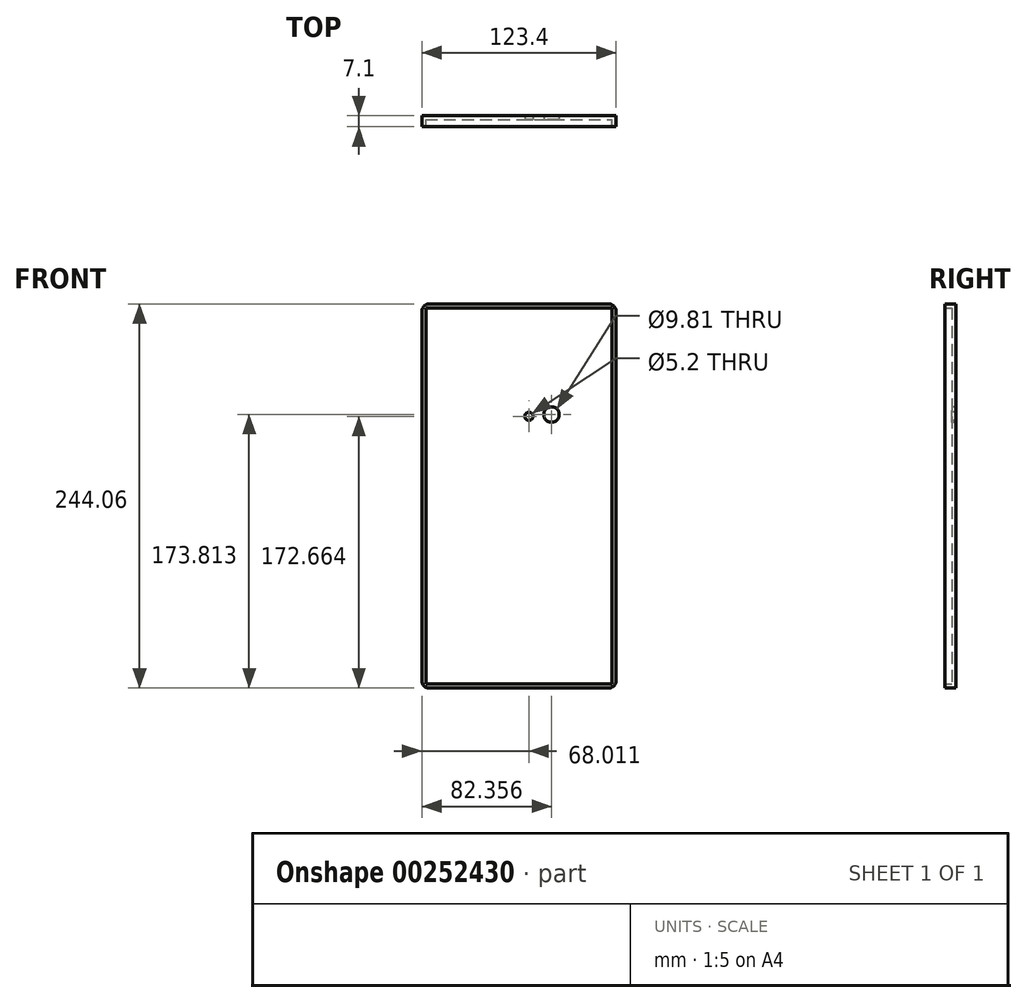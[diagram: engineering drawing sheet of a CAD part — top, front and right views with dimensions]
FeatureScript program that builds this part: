
annotation { "Feature Type Name" : "Feature", "Feature Type Description" : "" }
export const myFeature = defineFeature(function(context is Context, id is Id, definition is map)
    precondition{}
    {
        {
            var Q0;
            Q0=qCreatedBy(makeId("Front.planeOp"),FACE);
            var sketch = newSketch(context, id + "F0", { "sketchPlane" : qUnion([Q0])});
            skLineSegment(sketch, "E0.bottom", {"start": v(-61.7, 122.03) * mm, "end": v(61.7, 122.03) * mm});
            skLineSegment(sketch, "E0.top", {"start": v(-61.7, -122.03) * mm, "end": v(61.7, -122.03) * mm});
            skLineSegment(sketch, "E0.left", {"start": v(-61.7, 122.03) * mm, "end": v(-61.7, -122.03) * mm});
            skLineSegment(sketch, "E0.right", {"start": v(61.7, 122.03) * mm, "end": v(61.7, -122.03) * mm});
            skPoint(sketch, "E0.middle", {"position": v(0, 0) * mm});
            skSolve(sketch);
        }
        {
            var Q0;
            Q0=makeQuery(id+"F0.imprint","IMPRINT",FACE,{"disambiguationData":[TD([[makeQuery(id+"F0.imprint","IMPRINT",EDGE,{"derivedFrom":sQuery(id+"F0.wireOp",EDGE,"E0.bottom")}),-1.0]])]});
            extrude(context, id + "F1", {"entities" : qUnion([Q0]), "endBound" : BoundingType.SYMMETRIC, "depth" : 7.1 * mm});
        }
        {
            var Q0;
            Q0=makeQuery(id+"F1.opExtrude","CAP_FACE",FACE,{"disambiguationData":[OSD([sQuery(id+"F0.wireOp",EDGE,"E0.bottom"),sQuery(id+"F0.wireOp",EDGE,"E0.top"),sQuery(id+"F0.wireOp",EDGE,"E0.left"),sQuery(id+"F0.wireOp",EDGE,"E0.right")])],"isStart":false});
            shell(context, id + "F2", {"entities" : qUnion([Q0]), "thickness" : 2.54 * mm});
        }
        {
            var Q0;
            Q0=qCreatedBy(makeId("Front.planeOp"),FACE);
            var sketch = newSketch(context, id + "F3", { "sketchPlane" : qUnion([Q0])});
            skLineSegment(sketch, "E1.bottom", {"start": v(6.69, 50.63) * mm, "end": v(20.66, 50.63) * mm});
            skLineSegment(sketch, "E1.top", {"start": v(6.69, 50.63) * mm, "end": v(20.66, 50.63) * mm});
            skLineSegment(sketch, "E1.left", {"start": v(20.66, 50.63) * mm, "end": v(20.66, 50.63) * mm});
            skLineSegment(sketch, "E1.right", {"start": v(6.69, 50.63) * mm, "end": v(6.69, 50.63) * mm});
            skCircle(sketch, "E2", {"center": v(6.31, 50.63) * mm, "radius": 2.6 * mm});
            skPoint(sketch, "E2.centerSnap0", {"position": v(20.66, 50.63) * mm});
            skCircle(sketch, "E3", {"center": v(20.66, 51.78) * mm, "radius": 4.9 * mm});
            skSolve(sketch);
        }
        {
            var Q0;
            Q0=makeQuery(id+"F1.opExtrude","SWEPT_EDGE",EDGE,{"disambiguationData":[OSD([sQuery(id+"F0.wireOp",EDGE,"E0.bottom"),sQuery(id+"F0.wireOp",EDGE,"E0.right")])]});
            var Q1;
            Q1=makeQuery(id+"F1.opExtrude","SWEPT_EDGE",EDGE,{"disambiguationData":[OSD([sQuery(id+"F0.wireOp",EDGE,"E0.bottom"),sQuery(id+"F0.wireOp",EDGE,"E0.left")])]});
            var Q2;
            Q2=makeQuery(id+"F1.opExtrude","SWEPT_EDGE",EDGE,{"disambiguationData":[OSD([sQuery(id+"F0.wireOp",EDGE,"E0.top"),sQuery(id+"F0.wireOp",EDGE,"E0.left")])]});
            var Q3;
            Q3=makeQuery(id+"F1.opExtrude","SWEPT_EDGE",EDGE,{"disambiguationData":[OSD([sQuery(id+"F0.wireOp",EDGE,"E0.top"),sQuery(id+"F0.wireOp",EDGE,"E0.right")])]});
            fillet(context, id + "F4", {"entities" : qUnion([Q0, Q1, Q2, Q3]), "radius" : 5 * mm, "tangentPropagation" : true, "allowEdgeOverflow" : false});
        }
        {
            var Q0;
            Q0 = qSketchRegion(id + "F3", true);
            extrude(context, id + "F5", {"entities" : qUnion([Q0]), "operationType" : NewBodyOperationType.REMOVE, "oppositeDirection" : true, "depth" : 25 * mm});
        }
    });
